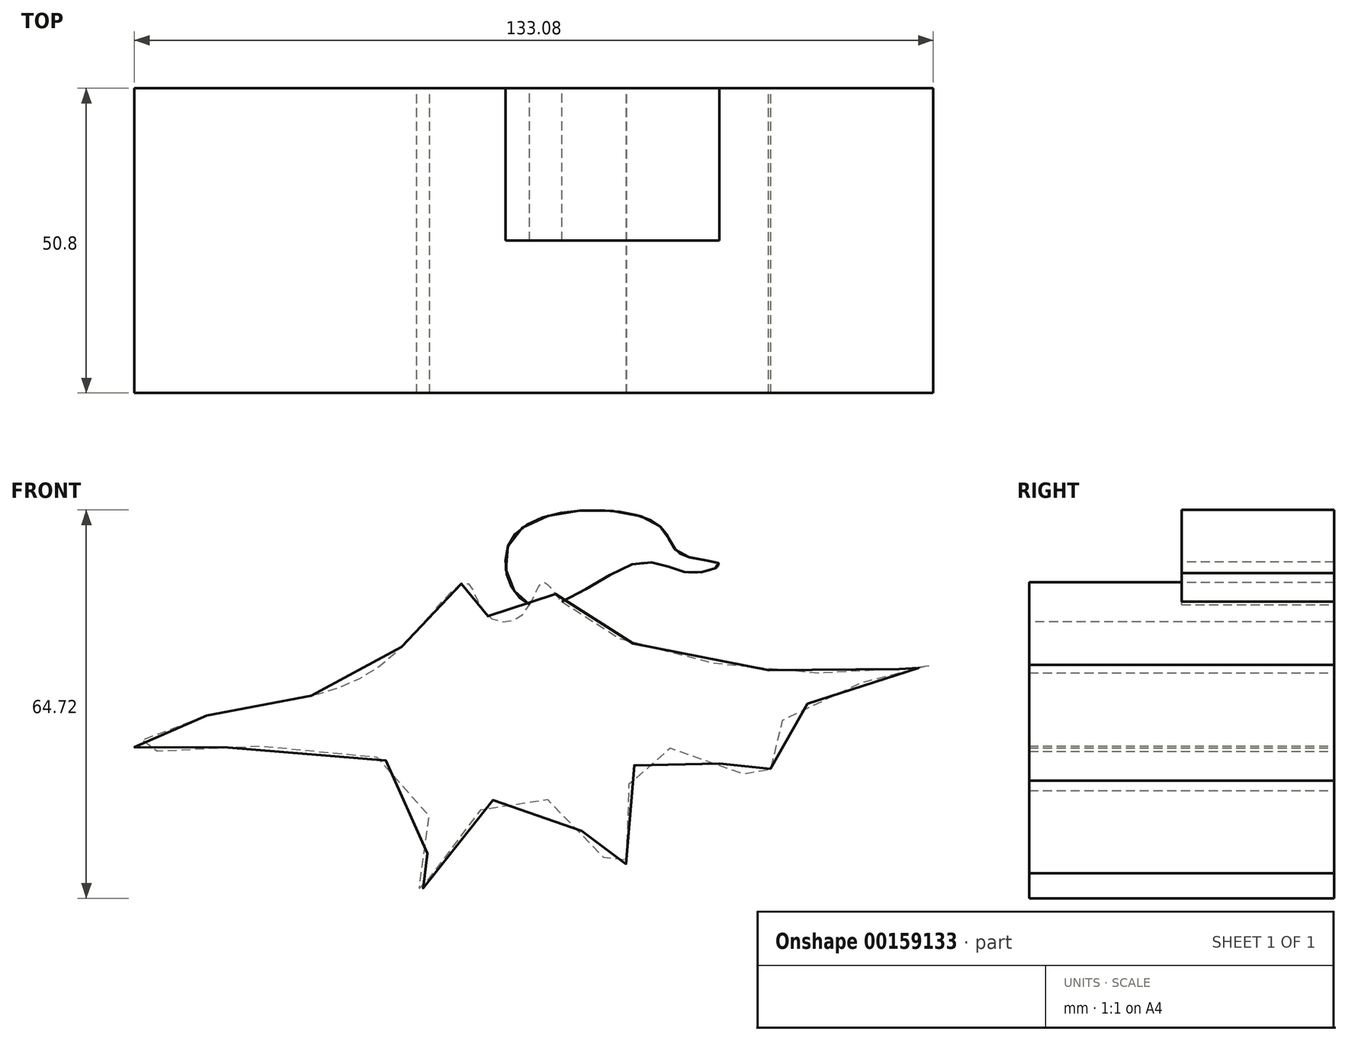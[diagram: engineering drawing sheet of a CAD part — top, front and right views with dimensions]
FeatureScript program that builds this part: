
annotation { "Feature Type Name" : "Feature", "Feature Type Description" : "" }
export const myFeature = defineFeature(function(context is Context, id is Id, definition is map)
    precondition{}
    {
        {
            var Q0;
            Q0=qCreatedBy(makeId("Front.planeOp"),FACE);
            var sketch = newSketch(context, id + "F0", { "sketchPlane" : qUnion([Q0])});
            skFitSpline(sketch, "E0", {"points": [v(-67.27, 16.59) * mm, v(-38.5, 24.84) * mm, v(-24.01, 38.77) * mm, v(-20.9, 33.64) * mm, v(-14.85, 33.27) * mm, v(-11.36, 38.77) * mm, v(-5.87, 33.45) * mm, v(38.5, 23.74) * mm, v(53.52, 25.02) * mm, v(27.13, 14.02) * mm, v(26.21, 5.77) * mm, v(5.5, 10.36) * mm, v(2.02, -9.62) * mm, v(-15.21, 4.12) * mm, v(-32.26, -13.84) * mm, v(-32.44, 5.77) * mm, v(-79, 10.9) * mm, v(-67.27, 16.59) * mm]});
            skSolve(sketch);
        }
        {
            var Q0;
            Q0=makeQuery(id+"F0.imprint","IMPRINT",FACE,{"disambiguationData":[TD([[makeQuery(id+"F0.imprint","IMPRINT",EDGE,{"derivedFrom":sQuery(id+"F0.wireOp",EDGE,"E0")}),-1.0]])]});
            extrude(context, id + "F1", {"entities" : qUnion([Q0]), "depth" : 25.4 * mm});
        }
        {
            var Q0;
            Q0=makeQuery(id+"F1.opExtrude","CAP_FACE",FACE,{"disambiguationData":[OSD([sQuery(id+"F0.wireOp",EDGE,"E0")])],"isStart":false});
            extrude(context, id + "F2", {"entities" : qUnion([Q0]), "operationType" : NewBodyOperationType.ADD, "depth" : 25.4 * mm});
        }
        {
            var Q0;
            Q0=qCreatedBy(makeId("Front.planeOp"),FACE);
            var sketch = newSketch(context, id + "F3", { "sketchPlane" : qUnion([Q0])});
            skFitSpline(sketch, "E1", {"points": [v(7.59, 48.71) * mm, v(-16.1, 46.63) * mm, v(-12.96, 34.93) * mm, v(4.5, 42.07) * mm, v(13.67, 40.38) * mm, v(18.13, 41.86) * mm, v(11.58, 43.62) * mm, v(7.59, 48.71) * mm]});
            skSolve(sketch);
        }
        {
            var Q0;
            Q0 = qSketchRegion(id + "F3", true);
            extrude(context, id + "F4", {"entities" : qUnion([Q0]), "operationType" : NewBodyOperationType.ADD, "depth" : 25.4 * mm});
        }
        {
            var Q0;
            Q0=qCreatedBy(makeId("Front.planeOp"),FACE);
            var sketch = newSketch(context, id + "F5", { "sketchPlane" : qUnion([Q0])});
            skSolve(sketch);
        }
        {
            var Q0;
            Q0 = qSketchRegion(id + "F5", true);
            var Q1;
            Q1=makeQuery(id+"F4.opExtrude","CAP_FACE",FACE,{"disambiguationData":[OSD([sQuery(id+"F3.wireOp",EDGE,"E1")])],"isStart":false});
            var Q2;
            Q2=makeQuery(id+"F2.opExtrude","CAP_FACE",FACE,{"disambiguationData":[OSD([sQuery(id+"F0.wireOp",EDGE,"E0")])],"isStart":false});
            extrude(context, id + "F6", {"entities" : qUnion([Q0, Q1, Q2]), "operationType" : NewBodyOperationType.ADD, "oppositeDirection" : true, "depth" : 25.4 * mm});
        }
    });
